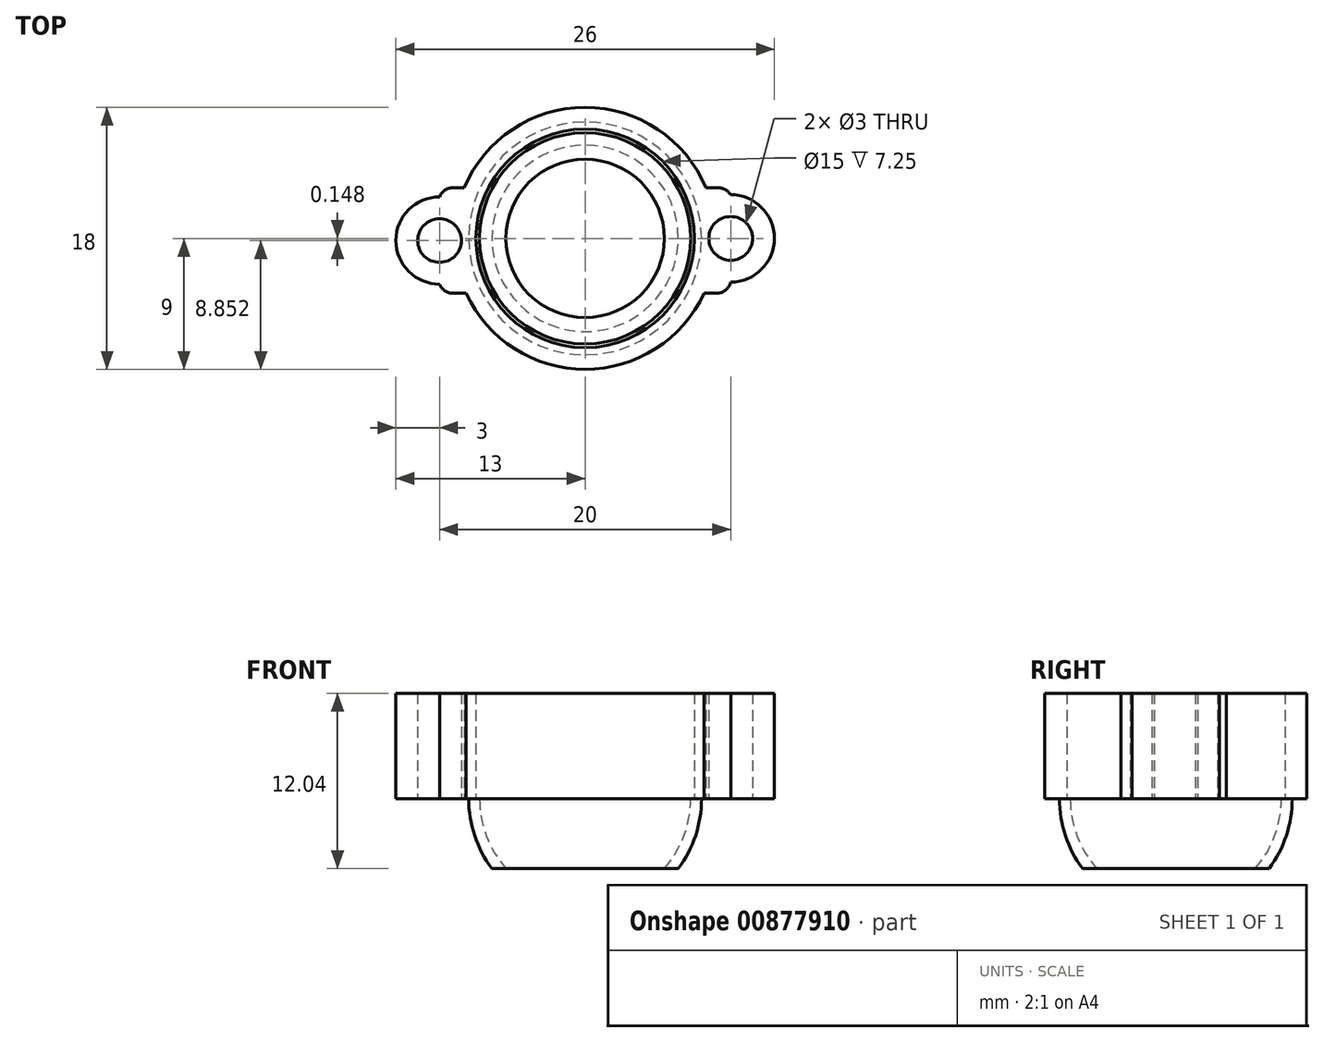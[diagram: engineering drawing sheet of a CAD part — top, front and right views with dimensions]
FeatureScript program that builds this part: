
annotation { "Feature Type Name" : "Feature", "Feature Type Description" : "" }
export const myFeature = defineFeature(function(context is Context, id is Id, definition is map)
    precondition{}
    {
        {
            var Q0;
            Q0=qCreatedBy(makeId("Top.planeOp"),FACE);
            var sketch = newSketch(context, id + "F0", { "sketchPlane" : qUnion([Q0])});
            skLineSegment(sketch, "E0.bottom", {"start": v(-10, 3.48) * mm, "end": v(-8.3, 3.48) * mm});
            skLineSegment(sketch, "E0.top", {"start": v(-10, -3.77) * mm, "end": v(-8.17, -3.77) * mm});
            skLineSegment(sketch, "E0.left", {"start": v(-10, 3.48) * mm, "end": v(-10, 2.85) * mm});
            skLineSegment(sketch, "E0.right", {"start": v(10, 3.48) * mm, "end": v(10, 3) * mm});
            skArc(sketch, "E1", {"start": v(-10, 2.85) * mm, "mid": v(-13, -0.15) * mm, "end": v(-10, -3.15) * mm});
            skArc(sketch, "E2", {"start": v(10, -3) * mm, "mid": v(13, 0) * mm, "end": v(10, 3) * mm});
            skArc(sketch, "E3", {"start": v(-8.17, -3.77) * mm, "mid": v(0, -9) * mm, "end": v(8.17, -3.77) * mm});
            skLineSegment(sketch, "E4.trimOffspring", {"start": v(-10, -3.15) * mm, "end": v(-10, -3.77) * mm});
            skLineSegment(sketch, "E5.trimOffspring", {"start": v(10, -3) * mm, "end": v(10, -3.77) * mm});
            skLineSegment(sketch, "E6.trimOffspring", {"start": v(8.3, 3.48) * mm, "end": v(10, 3.48) * mm});
            skLineSegment(sketch, "E7.trimOffspring", {"start": v(8.17, -3.77) * mm, "end": v(10, -3.77) * mm});
            skArc(sketch, "E8.trimOffspring", {"start": v(8.3, 3.48) * mm, "mid": v(0, 9) * mm, "end": v(-8.3, 3.48) * mm});
            skCircle(sketch, "E9", {"center": v(0, 0) * mm, "radius": 7.5 * mm});
            skCircle(sketch, "E10", {"center": v(-10, -0.15) * mm, "radius": 1.5 * mm});
            skCircle(sketch, "E11", {"center": v(10, 0) * mm, "radius": 1.5 * mm});
            skSolve(sketch);
        }
        {
            var Q0;
            Q0 = qSketchRegion(id + "F0", true);
            extrude(context, id + "F1", {"entities" : qUnion([Q0]), "depth" : 7.25 * mm, "offsetDistance" : 25 * mm});
        }
        {
            var Q0;
            Q0=qCreatedBy(makeId("Right.planeOp"),FACE);
            var sketch = newSketch(context, id + "F2", { "sketchPlane" : qUnion([Q0])});
            skArc(sketch, "E12", {"start": v(-8, 0) * mm, "mid": v(0, -8) * mm, "end": v(8, 0) * mm});
            skSolve(sketch);
        }
        {
            var Q0;
            Q0=makeQuery(id+"F1.opExtrude","CAP_FACE",FACE,{"disambiguationData":[OSD([sQuery(id+"F0.wireOp",EDGE,"E0.bottom"),sQuery(id+"F0.wireOp",EDGE,"E0.top"),sQuery(id+"F0.wireOp",EDGE,"E0.left"),sQuery(id+"F0.wireOp",EDGE,"E0.right"),sQuery(id+"F0.wireOp",EDGE,"E1"),sQuery(id+"F0.wireOp",EDGE,"E2"),sQuery(id+"F0.wireOp",EDGE,"E3"),sQuery(id+"F0.wireOp",EDGE,"E4.trimOffspring"),sQuery(id+"F0.wireOp",EDGE,"E5.trimOffspring")])],"isStart":true});
            var sketch = newSketch(context, id + "F3", { "sketchPlane" : qUnion([Q0])});
            skArc(sketch, "E13", {"start": v(-8, 0) * mm, "mid": v(0, -8) * mm, "end": v(8, 0) * mm});
            skLineSegment(sketch, "E14", {"start": v(-8, 0) * mm, "end": v(8, 0) * mm});
            skSolve(sketch);
        }
        {
            var Q0;
            Q0 = qSketchRegion(id + "F3", true);
            var Q1;
            Q1=sQuery(id+"F2.wireOp",EDGE,"E12");
            sweep(context, id + "F4", {"operationType" : NewBodyOperationType.ADD, "profiles" : qUnion([Q0]), "path" : qUnion([Q1])});
        }
        {
            var Q0;
            Q0=makeQuery(id+"F1.opExtrude","CAP_FACE",FACE,{"disambiguationData":[OSD([sQuery(id+"F0.wireOp",EDGE,"E0.bottom"),sQuery(id+"F0.wireOp",EDGE,"E0.top"),sQuery(id+"F0.wireOp",EDGE,"E0.left"),sQuery(id+"F0.wireOp",EDGE,"E0.right"),sQuery(id+"F0.wireOp",EDGE,"E1"),sQuery(id+"F0.wireOp",EDGE,"E2"),sQuery(id+"F0.wireOp",EDGE,"E3"),sQuery(id+"F0.wireOp",EDGE,"E4.trimOffspring"),sQuery(id+"F0.wireOp",EDGE,"E5.trimOffspring")])],"isStart":true});
            var sketch = newSketch(context, id + "F5", { "sketchPlane" : qUnion([Q0])});
            skArc(sketch, "E15", {"start": v(7.25, 0) * mm, "mid": v(0, 7.25) * mm, "end": v(-7.25, 0) * mm});
            skLineSegment(sketch, "E16", {"start": v(-7.25, 0) * mm, "end": v(7.25, 0) * mm});
            skSolve(sketch);
        }
        {
            var Q0;
            Q0=qCreatedBy(makeId("Right.planeOp"),FACE);
            var sketch = newSketch(context, id + "F6", { "sketchPlane" : qUnion([Q0])});
            skCircle(sketch, "E17", {"center": v(0, 0) * mm, "radius": 7.25 * mm});
            skSolve(sketch);
        }
        {
            var Q0;
            Q0 = qSketchRegion(id + "F5", true);
            var Q1;
            Q1=sQuery(id+"F6.wireOp",EDGE,"E17");
            sweep(context, id + "F7", {"operationType" : NewBodyOperationType.REMOVE, "profiles" : qUnion([Q0]), "path" : qUnion([Q1])});
        }
        {
            var Q0;
            Q0=qCreatedBy(makeId("Front.planeOp"),FACE);
            var sketch = newSketch(context, id + "F8", { "sketchPlane" : qUnion([Q0])});
            skLineSegment(sketch, "E18.bottom", {"start": v(11.67, -4.8) * mm, "end": v(-11.06, -4.8) * mm});
            skLineSegment(sketch, "E18.top", {"start": v(11.67, -10.6) * mm, "end": v(-11.06, -10.6) * mm});
            skLineSegment(sketch, "E18.left", {"start": v(11.67, -4.8) * mm, "end": v(11.67, -10.6) * mm});
            skLineSegment(sketch, "E18.right", {"start": v(-11.06, -4.8) * mm, "end": v(-11.06, -10.6) * mm});
            skSolve(sketch);
        }
        {
            var Q0;
            Q0 = qSketchRegion(id + "F8", true);
            extrude(context, id + "F9", {"entities" : qUnion([Q0]), "operationType" : NewBodyOperationType.REMOVE, "depth" : 25 * mm, "offsetDistance" : 25 * mm, "hasSecondDirection" : true, "secondDirectionOppositeDirection" : true, "secondDirectionDepth" : 25 * mm});
        }
        {
            var Q0;
            Q0=makeQuery(id+"F1.opExtrude","SWEPT_EDGE",EDGE,{"disambiguationData":[OSD([sQuery(id+"F0.wireOp",EDGE,"E0.bottom"),sQuery(id+"F0.wireOp",EDGE,"E0.left")])]});
            var Q1;
            Q1=makeQuery(id+"F1.opExtrude","SWEPT_EDGE",EDGE,{"disambiguationData":[OSD([sQuery(id+"F0.wireOp",EDGE,"E0.top"),sQuery(id+"F0.wireOp",EDGE,"E4.trimOffspring")])]});
            var Q2;
            Q2=makeQuery(id+"F1.opExtrude","SWEPT_EDGE",EDGE,{"disambiguationData":[OSD([sQuery(id+"F0.wireOp",EDGE,"E5.trimOffspring"),sQuery(id+"F0.wireOp",EDGE,"E7.trimOffspring")])]});
            var Q3;
            Q3=makeQuery(id+"F1.opExtrude","SWEPT_EDGE",EDGE,{"disambiguationData":[OSD([sQuery(id+"F0.wireOp",EDGE,"E0.right"),sQuery(id+"F0.wireOp",EDGE,"E6.trimOffspring")])]});
            fillet(context, id + "F10", {"entities" : qUnion([Q0, Q1, Q2, Q3]), "radius" : 1 * mm, "tangentPropagation" : true, "allowEdgeOverflow" : false});
        }
    });
